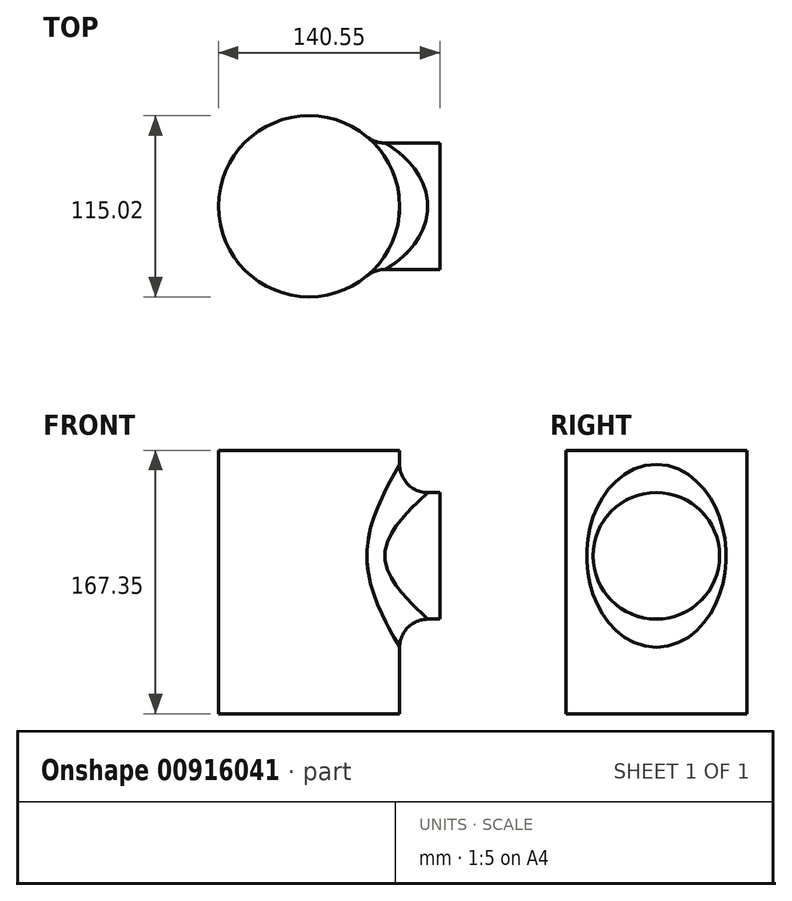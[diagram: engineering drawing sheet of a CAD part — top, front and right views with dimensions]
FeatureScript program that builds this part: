
annotation { "Feature Type Name" : "Feature", "Feature Type Description" : "" }
export const myFeature = defineFeature(function(context is Context, id is Id, definition is map)
    precondition{}
    {
        {
            var Q0;
            Q0=qCreatedBy(makeId("Top.planeOp"),FACE);
            var sketch = newSketch(context, id + "F0", { "sketchPlane" : qUnion([Q0])});
            skCircle(sketch, "E0", {"center": v(0, 0) * mm, "radius": 57.5 * mm});
            skSolve(sketch);
        }
        {
            var Q0;
            Q0 = qSketchRegion(id + "F0", true);
            extrude(context, id + "F1", {"entities" : qUnion([Q0]), "depth" : 167.35 * mm, "offsetDistance" : 25.4 * mm});
        }
        {
            var Q0;
            Q0=qCreatedBy(makeId("Right.planeOp"),FACE);
            cPlane(context, id + "F2", {"entities" : qUnion([Q0]), "cplaneType" : CPlaneType.OFFSET, "offset" : 83.04 * mm, "width" : 152.4 * mm, "height" : 152.4 * mm});
        }
        {
            var Q0;
            Q0=qCreatedBy(id+"F2.planeOp",FACE);
            var sketch = newSketch(context, id + "F3", { "sketchPlane" : qUnion([Q0])});
            skLineSegment(sketch, "E1", {"start": v(0, 0) * mm, "end": v(0, 156.33) * mm, "construction": true});
            skCircle(sketch, "E2", {"center": v(0, 100.3) * mm, "radius": 40.18 * mm});
            skSolve(sketch);
        }
        {
            var Q0;
            Q0=makeQuery(id+"F3.imprint","IMPRINT",FACE,{"disambiguationData":[TD([[makeQuery(id+"F3.imprint","IMPRINT",EDGE,{"derivedFrom":sQuery(id+"F3.wireOp",EDGE,"E2")}),1.0]])]});
            var Q1;
            Q1=sQuery(id+"F3.wireOp",EDGE,"E2");
            extrude(context, id + "F4", {"entities" : qUnion([Q0]), "operationType" : NewBodyOperationType.ADD, "surfaceEntities" : qUnion([Q1]), "oppositeDirection" : true, "depth" : 54.2 * mm, "offsetDistance" : 25.4 * mm});
        }
        {
            var Q0;
            Q0=makeQuery(id+"F4.boolean.opBoolean","INTERSECT",EDGE,{"derivedFrom":[makeQuery(id+"F1.opExtrude","SWEPT_FACE",FACE,{"disambiguationData":[OSD([sQuery(id+"F0.wireOp",EDGE,"E0")])]}),makeQuery(id+"F4.opExtrude","SWEPT_FACE",FACE,{"disambiguationData":[OSD([sQuery(id+"F3.wireOp",EDGE,"E2")])]})]});
            fillet(context, id + "F5", {"entities" : qUnion([Q0]), "radius" : 17.91 * mm, "tangentPropagation" : true, "allowEdgeOverflow" : false});
        }
    });
